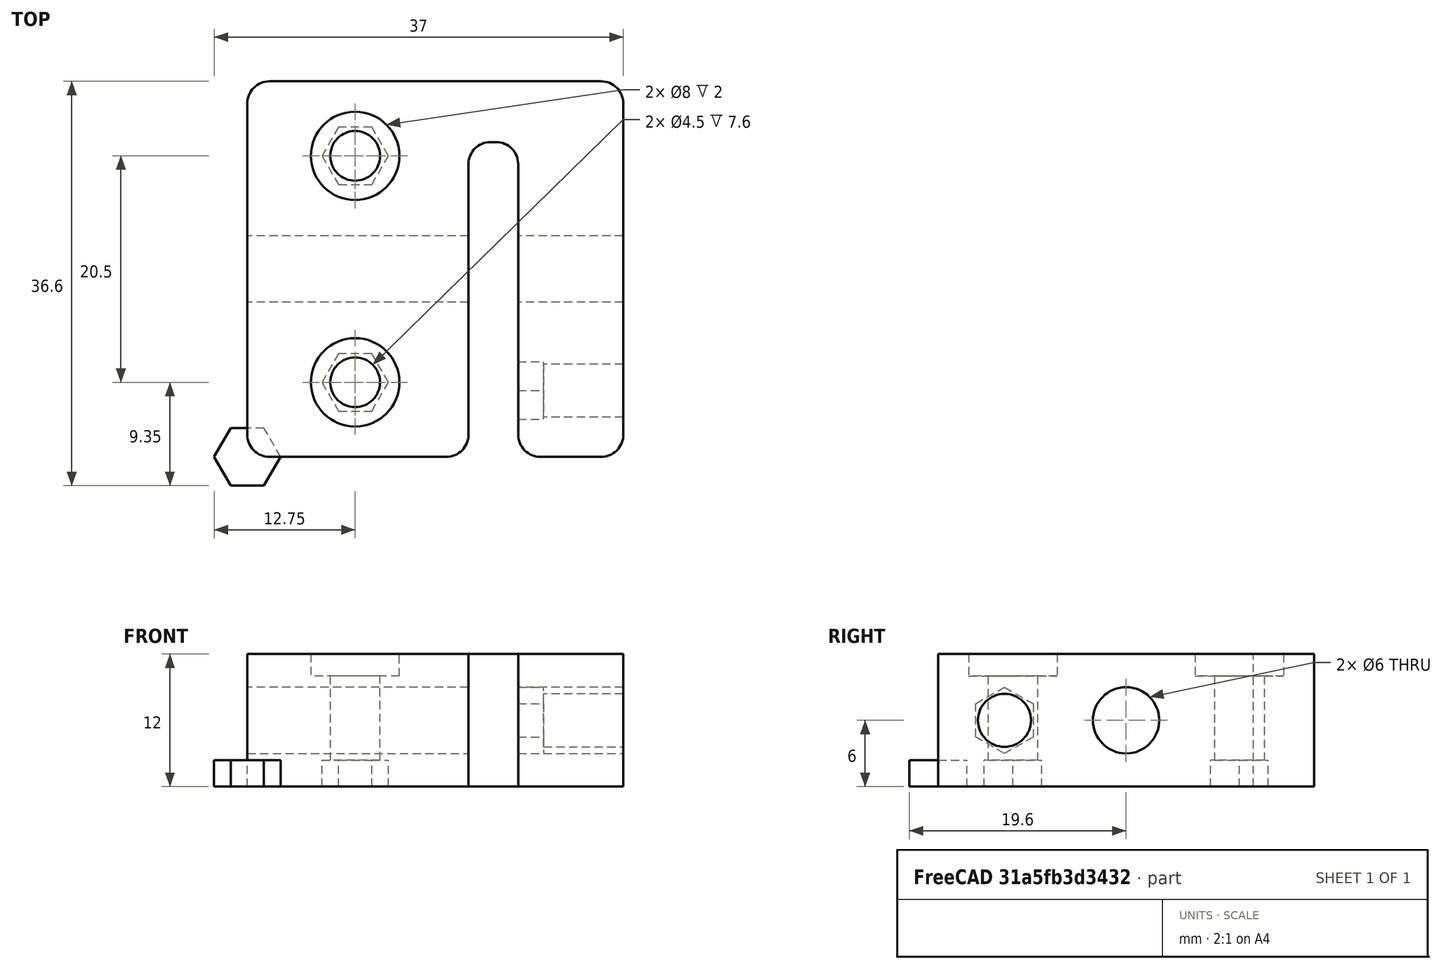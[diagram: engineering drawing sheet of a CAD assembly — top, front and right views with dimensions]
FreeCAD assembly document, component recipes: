
FREECAD ASSEMBLY — COMPONENT RECIPES ("AntiBacklashNutT8")

This assembly document has 3 components, labeled P0..P2 below (a component is one placed body or linked part). 0 of them carry a construction recipe — the FreeCAD feature program that regenerates the part from scratch, quoted from this document or its linked companion documents; the rest are supplied as boundary geometry only. No exploded tour is included for this assembly.
COMPONENT P0 — geometry summary ("DIN934_M4"; no construction recipe available for this part):
  bounding box: 6.0 x 5.2 x 2.4 mm
  tessellated surface: 20 triangles
  volume: 56 mm^3 (75% of its bounding box)
  symmetry: 2-fold rotationally symmetric about the x axis; 2-fold rotationally symmetric about the y axis; 6-fold rotationally symmetric about the z axis; mirror-symmetric across its x mid-plane, y mid-plane
COMPONENT P1 — geometry summary ("DIN934_M006"; no construction recipe available for this part):
  bounding box: 6.0 x 5.2 x 2.4 mm
  tessellated surface: 20 triangles
  volume: 56 mm^3 (75% of its bounding box)
  symmetry: 2-fold rotationally symmetric about the x axis; 2-fold rotationally symmetric about the y axis; 6-fold rotationally symmetric about the z axis; mirror-symmetric across its x mid-plane, y mid-plane
COMPONENT P2 — geometry summary ("DIN934_M007"; no construction recipe available for this part):
  bounding box: 6.0 x 5.2 x 2.4 mm
  tessellated surface: 20 triangles
  volume: 56 mm^3 (75% of its bounding box)
  symmetry: 2-fold rotationally symmetric about the x axis; 2-fold rotationally symmetric about the y axis; 6-fold rotationally symmetric about the z axis; mirror-symmetric across its x mid-plane, y mid-plane
PROVENANCE & LICENSES
A FreeCAD (.FCStd) document from a public repository crawl; recipes are the document's own serialized feature recipes (and, for linked parts, companion documents' recipes).
License: bsd.
